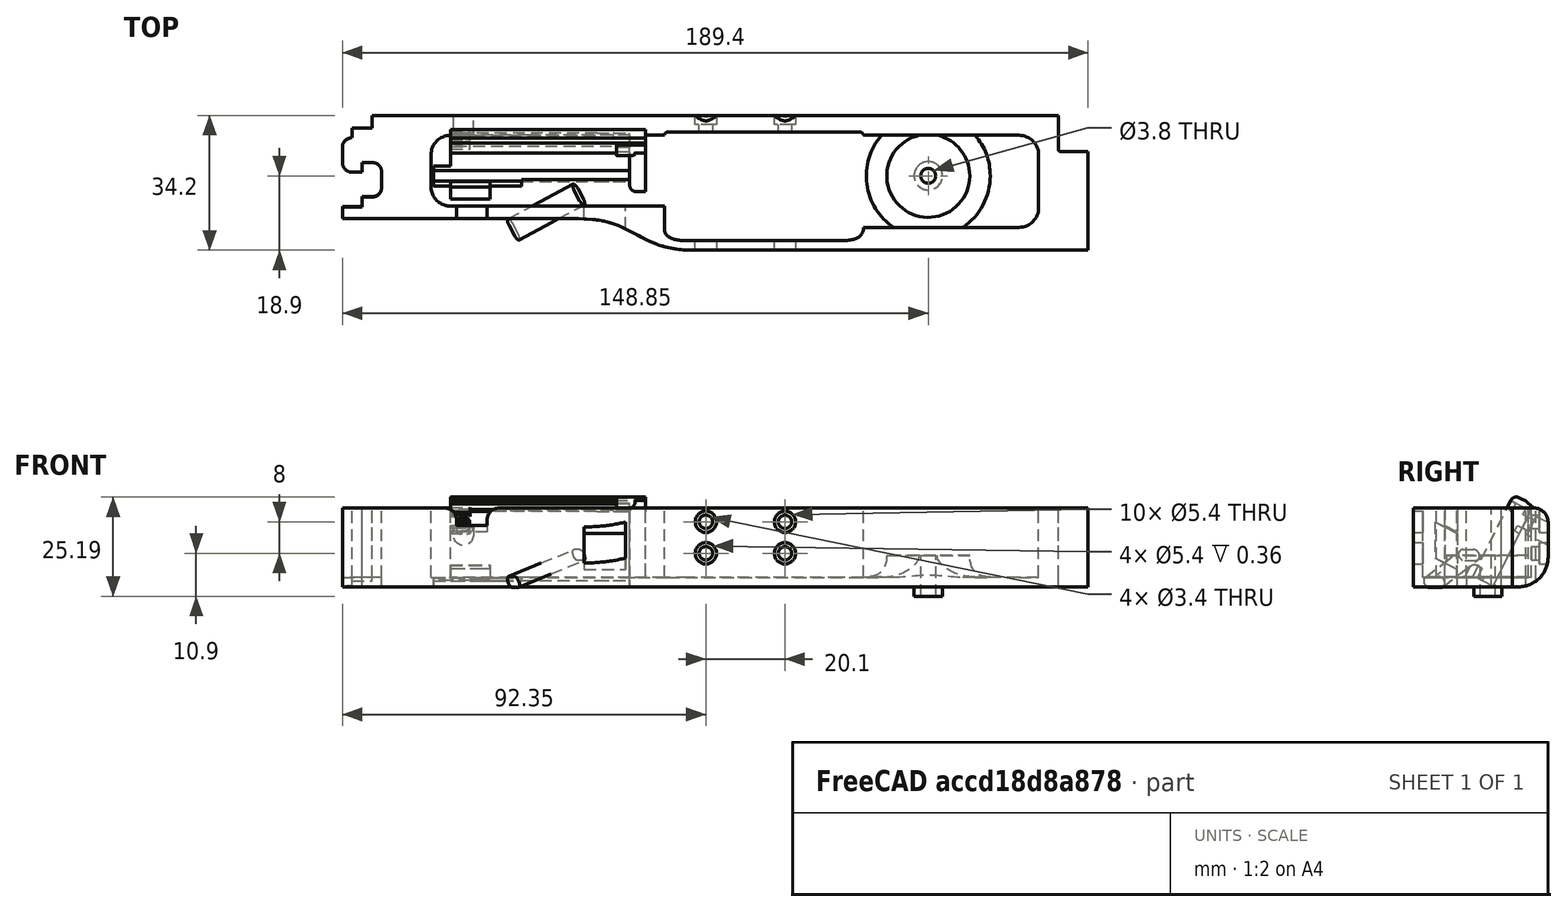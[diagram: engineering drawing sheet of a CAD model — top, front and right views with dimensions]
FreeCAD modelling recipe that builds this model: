
FCSTD DOCUMENT  (FreeCAD 0.19R0.19.2)
Label: v0_996
License: All rights reserved
LicenseURL: http://en.wikipedia.org/wiki/All_rights_reserved
objects: Sketcher::SketchObject×37, Part::Extrusion×31, Part::MultiFuse×19, Part::Box×14, Part::Cut×14, Part::Fillet×13, App::MeasureDistance×4, Part::Cylinder×4, Part::Revolution×1, Mesh::Feature×1
note: 133 computed .brp shape members not serialized (recipe doc carries the construction recipe); baked Part::Feature solids carry a one-line shape summary decoded from their .brp

FEATURE [Sketcher::SketchObject] Sketch
  FullyConstrained = true
  sketch-geometry (36):
    g0: LineSegment StartX=0 StartY=0 StartZ=0 EndX=154.4 EndY=0 EndZ=0
    g1: LineSegment StartX=154.4 StartY=0 StartZ=0 EndX=154.4 EndY=-7.6 EndZ=0
    g2: LineSegment StartX=32.5209 StartY=-26.2 StartZ=0 EndX=-7.5 EndY=-26.2 EndZ=0
    g3-g7: Circle x5 (B-spline internal-alignment scaffolding for g8; pole/knot coordinates omitted)
    g8: BSplineCurve PolesCount=5 KnotsCount=3 Degree=3 IsPeriodic=0
    g9: GeomPoint X=61.85 Y=-33.8 Z=0
    g10: GeomPoint X=47.185 Y=-29.9 Z=0
    g11: GeomPoint X=32.5209 Y=-26.2 Z=0
    g12: Circle CenterX=121.35 CenterY=-14.3 CenterZ=0 NormalX=0 NormalY=0 NormalZ=1 AngleXU=0 Radius=3.25
    g13: LineSegment StartX=-7.5 StartY=-26.2 StartZ=0 EndX=-27.5 EndY=-26.2 EndZ=0
    g14: LineSegment StartX=-20 StartY=0 StartZ=0 EndX=0 EndY=0 EndZ=0
    g15: LineSegment StartX=-25 StartY=-3.1 StartZ=0 EndX=-20 EndY=-3.1 EndZ=0
    g16: LineSegment StartX=-25 StartY=-3.1 StartZ=0 EndX=-25 EndY=-5.6 EndZ=0
    g17: LineSegment StartX=-27.5 StartY=-8.1 StartZ=0 EndX=-27.5 EndY=-11.85 EndZ=0
    g18: ArcOfCircle CenterX=-25 CenterY=-8.1 CenterZ=0 NormalX=0 NormalY=0 NormalZ=1 AngleXU=0 Radius=2.5 StartAngle=1.5708 EndAngle=3.14159
    g19: LineSegment StartX=-25 StartY=-14.35 StartZ=0 EndX=-22.5 EndY=-14.35 EndZ=0
    g20: ArcOfCircle CenterX=-25 CenterY=-11.85 CenterZ=0 NormalX=0 NormalY=0 NormalZ=1 AngleXU=0 Radius=2.5 StartAngle=3.14159 EndAngle=4.71239
    g21: LineSegment StartX=-22.5 StartY=-14.35 StartZ=0 EndX=-22.5 EndY=-11.85 EndZ=0
    g22: LineSegment StartX=-22.5 StartY=-11.85 StartZ=0 EndX=-20 EndY=-11.85 EndZ=0
    g23: ArcOfCircle CenterX=-20 CenterY=-14.35 CenterZ=0 NormalX=0 NormalY=0 NormalZ=1 AngleXU=0 Radius=2.5 StartAngle=8e-16 EndAngle=1.5708
    g24: LineSegment StartX=-17.5 StartY=-14.35 StartZ=0 EndX=-17.5 EndY=-18.1 EndZ=0
    g25: ArcOfCircle CenterX=-20 CenterY=-18.1 CenterZ=0 NormalX=0 NormalY=0 NormalZ=1 AngleXU=0 Radius=2.5 StartAngle=4.71239 EndAngle=6.28319
    g26: LineSegment StartX=-22.5 StartY=-20.6 StartZ=0 EndX=-20 EndY=-20.6 EndZ=0
    g27: LineSegment StartX=-22.5 StartY=-20.6 StartZ=0 EndX=-22.5 EndY=-23.1 EndZ=0
    g28: LineSegment StartX=-27.5 StartY=-23.1 StartZ=0 EndX=-22.5 EndY=-23.1 EndZ=0
    g29: LineSegment StartX=-20 StartY=-3.1 StartZ=0 EndX=-20 EndY=0 EndZ=0
    g30: LineSegment StartX=-27.5 StartY=-23.1 StartZ=0 EndX=-27.5 EndY=-26.2 EndZ=0
    g31: LineSegment StartX=154.4 StartY=-7.6 StartZ=0 EndX=154.4 EndY=-8.6 EndZ=0
    g32: ArcOfCircle CenterX=154.9 CenterY=-8.6 CenterZ=0 NormalX=0 NormalY=0 NormalZ=1 AngleXU=0 Radius=0.5 StartAngle=3.14159 EndAngle=4.71239
    g33: LineSegment StartX=154.9 StartY=-9.1 StartZ=0 EndX=161.9 EndY=-9.1 EndZ=0
    g34: LineSegment StartX=161.9 StartY=-9.1 StartZ=0 EndX=161.9 EndY=-33.8 EndZ=0
    g35: LineSegment StartX=161.9 StartY=-33.8 StartZ=0 EndX=61.85 EndY=-33.8 EndZ=0
  constraints (72):
    c: PointOnObject(g0,g-2)
    c: Horizontal(g0)
    c: Distance(g0) = 154.4
    c: DistanceY(g-1,g0) = 0
    c: Vertical(g1)
    c: Distance(g1) = 7.6
    c: Coincident(g1,g0)
    c: Horizontal(g2)
    c: Block(g2)
    c: Weight(g3) = 1
    c: Coincident(g8,g2)
    c: InternalAlignment(g3-g7 -> g8) x5
    c: InternalAlignment(g9,g8)
    c: InternalAlignment(g10,g8)
    c: InternalAlignment(g11,g8)
    c: Block(g12)
    c: Coincident(g13,g2)
    c: Horizontal(g13)
    c: Distance(g13) = 20
    c: Horizontal(g14)
    c: Distance(g14) = 20
    c: Coincident(g14,g0)
    c: Horizontal(g15)
    c: Vertical(g16)
    c: Coincident(g16,g15)
    c: Vertical(g17)
    c: Coincident(g18,g16)
    c: Block(g18)
    c: Coincident(g17,g18)
    c: Horizontal(g19)
    c: Coincident(g20,g17)
    c: Block(g20)
    c: Block(g19)
    c: Vertical(g21)
    c: Coincident(g21,g19)
    c: Horizontal(g22)
    c: Coincident(g22,g21)
    c: Coincident(g23,g22)
    c: Vertical(g24)
    c: Block(g23)
    c: Coincident(g24,g23)
    c: Coincident(g25,g24)
    c: Block(g25)
    c: Horizontal(g26)
    c: Coincident(g26,g25)
    c: Vertical(g27)
    c: Coincident(g27,g26)
    c: Horizontal(g28)
    c: Coincident(g28,g27)
    c: Block(g15)
    c: Block(g28)
    c: Coincident(g29,g15)
    c: Coincident(g29,g14)
    c: Vertical(g29)
    c: Coincident(g30,g28)
    c: Coincident(g30,g13)
    c: Vertical(g30)
    c: Vertical(g31)
    c: Distance(g31) = 1
    c: Coincident(g31,g1)
    c: Coincident(g32,g31)
    c: Block(g32)
    c: Coincident(g33,g32)
    c: Horizontal(g33)
    c: Coincident(g34,g33)
    c: Vertical(g34)
    c: Block(g34)
    c: Coincident(g35,g34)
    c: Horizontal(g35)
    c: Block(g35)
    c: Coincident(g8,g35)
    c: Block(g8)
FEATURE [Part::Extrusion] Extrude  label="mainBodyBaseExtrude"
  Base = -> Sketch
  Dir = (0,0,1)
  DirMode = 2
  FaceMakerClass = Part::FaceMakerBullseye
  LengthFwd = 2.4
  LengthRev = 0
  Solid = true
  Symmetric = false
FEATURE [Sketcher::SketchObject] Sketch001
  FullyConstrained = true
  sketch-geometry (75):
    g0: ArcOfCircle CenterX=144.4 CenterY=-10 CenterZ=0 NormalX=0 NormalY=0 NormalZ=1 AngleXU=0 Radius=5 StartAngle=4.345e-13 EndAngle=1.5708
    g1: LineSegment StartX=32.5209 StartY=-26.2 StartZ=0 EndX=-7.49911 EndY=-26.2 EndZ=0
    g2: LineSegment StartX=0 StartY=0 StartZ=0 EndX=154.4 EndY=0 EndZ=0
    g3-g7: Circle x5 (B-spline internal-alignment scaffolding for g8; pole/knot coordinates omitted)
    g8: BSplineCurve PolesCount=5 KnotsCount=3 Degree=3 IsPeriodic=0
    g9: GeomPoint X=61.85 Y=-33.8 Z=0
    g10: GeomPoint X=47.1857 Y=-29.9 Z=0
    g11: GeomPoint X=32.5209 Y=-26.2 Z=0
    g12: LineSegment StartX=154.4 StartY=0 StartZ=0 EndX=154.4 EndY=-7.6 EndZ=0
    g13: LineSegment StartX=20 StartY=-5 StartZ=0 EndX=54.35 EndY=-5 EndZ=0
    g14: LineSegment StartX=104.85 StartY=-5 StartZ=0 EndX=144.4 EndY=-5 EndZ=0
    g15: LineSegment StartX=54.35 StartY=-23 StartZ=0 EndX=20 EndY=-23 EndZ=0
    g16: LineSegment StartX=-27.4991 StartY=-26.2 StartZ=0 EndX=-7.49911 EndY=-26.2 EndZ=0
    g17: LineSegment StartX=-20 StartY=0 StartZ=0 EndX=0 EndY=0 EndZ=0
    g18: LineSegment StartX=-27.4991 StartY=-23.2 StartZ=0 EndX=-22.5 EndY=-23.2 EndZ=0
    g19: LineSegment StartX=-22.5 StartY=-20.7 StartZ=0 EndX=-22.5 EndY=-23.2 EndZ=0
    g20: LineSegment StartX=-22.5 StartY=-20.7 StartZ=0 EndX=-20 EndY=-20.7 EndZ=0
    g21: ArcOfCircle CenterX=-20 CenterY=-18.2 CenterZ=0 NormalX=0 NormalY=0 NormalZ=1 AngleXU=0 Radius=2.5 StartAngle=4.71239 EndAngle=6.28319
    g22: LineSegment StartX=-17.5 StartY=-14.4 StartZ=0 EndX=-17.5 EndY=-18.2 EndZ=0
    g23: ArcOfCircle CenterX=-20 CenterY=-14.4 CenterZ=0 NormalX=0 NormalY=0 NormalZ=1 AngleXU=0 Radius=2.5 StartAngle=9e-16 EndAngle=1.5708
    g24: LineSegment StartX=-22.5 StartY=-11.9 StartZ=0 EndX=-20 EndY=-11.9 EndZ=0
    g25: LineSegment StartX=-22.5 StartY=-14.4 StartZ=0 EndX=-22.5 EndY=-11.9 EndZ=0
    g26: LineSegment StartX=-25 StartY=-14.4 StartZ=0 EndX=-22.5 EndY=-14.4 EndZ=0
    g27: ArcOfCircle CenterX=-25 CenterY=-11.9 CenterZ=0 NormalX=0 NormalY=0 NormalZ=1 AngleXU=0 Radius=2.5 StartAngle=3.14159 EndAngle=4.71239
    g28: LineSegment StartX=-27.5 StartY=-8.1 StartZ=0 EndX=-27.5 EndY=-11.9 EndZ=0
    g29: ArcOfCircle CenterX=-25 CenterY=-8.1 CenterZ=0 NormalX=0 NormalY=0 NormalZ=1 AngleXU=0 Radius=2.5 StartAngle=1.5708 EndAngle=3.14159
    g30: LineSegment StartX=-25 StartY=-3.1 StartZ=0 EndX=-25 EndY=-5.6 EndZ=0
    g31: LineSegment StartX=-20 StartY=-3.1 StartZ=0 EndX=-25 EndY=-3.1 EndZ=0
    g32: LineSegment StartX=-20 StartY=0 StartZ=0 EndX=-20 EndY=-3.1 EndZ=0
    g33: LineSegment StartX=-27.4991 StartY=-26.2 StartZ=0 EndX=-27.4991 EndY=-23.2 EndZ=0
    g34: LineSegment StartX=4.09e-14 StartY=-5 StartZ=0 EndX=20 EndY=-5 EndZ=0
    g35: ArcOfCircle CenterX=7.1e-15 CenterY=-18 CenterZ=0 NormalX=0 NormalY=0 NormalZ=1 AngleXU=0 Radius=5 StartAngle=3.14159 EndAngle=4.71239
    g36: ArcOfCircle CenterX=4.26e-14 CenterY=-10 CenterZ=0 NormalX=0 NormalY=0 NormalZ=1 AngleXU=0 Radius=5 StartAngle=1.5708 EndAngle=3.14159
    g37: LineSegment StartX=-5 StartY=-18 StartZ=0 EndX=-5 EndY=-10 EndZ=0
    g38: LineSegment StartX=6.2e-15 StartY=-23 StartZ=0 EndX=20 EndY=-23 EndZ=0
    g39: LineSegment StartX=154.4 StartY=-7.6 StartZ=0 EndX=154.4 EndY=-8.6 EndZ=0
    g40: LineSegment StartX=154.9 StartY=-9.1 StartZ=0 EndX=161.9 EndY=-9.1 EndZ=0
    g41: ArcOfCircle CenterX=154.9 CenterY=-8.6 CenterZ=0 NormalX=0 NormalY=0 NormalZ=1 AngleXU=0 Radius=0.5 StartAngle=3.14159 EndAngle=4.71299
    g42: LineSegment StartX=104.85 StartY=-28.3916 StartZ=0 EndX=144.408 EndY=-28.3916 EndZ=0
    g43: LineSegment StartX=149.4 StartY=-10 StartZ=0 EndX=149.4 EndY=-23.4 EndZ=0
    g44: ArcOfCircle CenterX=144.408 CenterY=-23.4 CenterZ=0 NormalX=0 NormalY=0 NormalZ=1 AngleXU=0 Radius=4.99164 StartAngle=4.71239 EndAngle=6.28319
    g45: LineSegment StartX=104.85 StartY=-28.3916 StartZ=0 EndX=104.85 EndY=-28.7833 EndZ=0
    g46: LineSegment StartX=54.35 StartY=-28.7916 StartZ=0 EndX=54.35 EndY=-23 EndZ=0
    g47: LineSegment StartX=161.9 StartY=-33.8 StartZ=0 EndX=161.9 EndY=-9.1 EndZ=0
    g48: LineSegment StartX=61.85 StartY=-33.8 StartZ=0 EndX=161.9 EndY=-33.8 EndZ=0
    g49: Circle CenterX=54.35 CenterY=-28.7916 CenterZ=0 NormalX=0 NormalY=0 NormalZ=1 AngleXU=0 Radius=1
    g50: Circle CenterX=54.35 CenterY=-31.7916 CenterZ=0 NormalX=0 NormalY=0 NormalZ=1 AngleXU=0 Radius=1
    g51: Circle CenterX=57.35 CenterY=-31.7916 CenterZ=0 NormalX=0 NormalY=0 NormalZ=1 AngleXU=0 Radius=1
    g52: BSplineCurve PolesCount=3 KnotsCount=2 Degree=2 IsPeriodic=0
    g53: GeomPoint X=54.35 Y=-28.7916 Z=0
    g54: GeomPoint X=57.35 Y=-31.7916 Z=0
    g55: Circle CenterX=104.85 CenterY=-28.7833 CenterZ=0 NormalX=0 NormalY=0 NormalZ=1 AngleXU=0 Radius=1
    g56: Circle CenterX=104.85 CenterY=-31.7916 CenterZ=0 NormalX=0 NormalY=0 NormalZ=1 AngleXU=0 Radius=1
    g57: Circle CenterX=101.85 CenterY=-31.7916 CenterZ=0 NormalX=0 NormalY=0 NormalZ=1 AngleXU=0 Radius=1
    g58: BSplineCurve PolesCount=3 KnotsCount=2 Degree=2 IsPeriodic=0
    g59: GeomPoint X=104.85 Y=-28.7833 Z=0
    g60: GeomPoint X=101.85 Y=-31.7916 Z=0
    g61: LineSegment StartX=57.35 StartY=-31.7916 StartZ=0 EndX=101.85 EndY=-31.7916 EndZ=0
    g62: Circle CenterX=54.35 CenterY=-5 CenterZ=0 NormalX=0 NormalY=0 NormalZ=1 AngleXU=0 Radius=1
    g63: Circle CenterX=54.35 CenterY=-4 CenterZ=0 NormalX=0 NormalY=0 NormalZ=1 AngleXU=0 Radius=1
    g64: Circle CenterX=55.15 CenterY=-4 CenterZ=0 NormalX=0 NormalY=0 NormalZ=1 AngleXU=0 Radius=1
    g65: BSplineCurve PolesCount=3 KnotsCount=2 Degree=2 IsPeriodic=0
    g66: GeomPoint X=54.35 Y=-5 Z=0
    g67: GeomPoint X=55.15 Y=-4 Z=0
    g68: Circle CenterX=104.85 CenterY=-5 CenterZ=0 NormalX=0 NormalY=0 NormalZ=1 AngleXU=0 Radius=1
    g69: Circle CenterX=104.85 CenterY=-4 CenterZ=0 NormalX=0 NormalY=0 NormalZ=1 AngleXU=0 Radius=1
    g70: Circle CenterX=104.05 CenterY=-4 CenterZ=0 NormalX=0 NormalY=0 NormalZ=1 AngleXU=0 Radius=1
    g71: BSplineCurve PolesCount=3 KnotsCount=2 Degree=2 IsPeriodic=0
    g72: GeomPoint X=104.85 Y=-5 Z=0
    g73: GeomPoint X=104.05 Y=-4 Z=0
    g74: LineSegment StartX=104.05 StartY=-4 StartZ=0 EndX=55.15 EndY=-4 EndZ=0
  constraints (156):
    c: PointOnObject(g2,g-2)
    c: DistanceY(g-1,g2) = 0
    c: Block(g0)
    c: Horizontal(g1)
    c: Distance(g1) = 40.02
    c: Horizontal(g2)
    c: Block(g2)
    c: Weight(g3) = 1
    c: Equal(g3, g4-g7) x4
    c: Coincident(g8,g1)
    c: InternalAlignment(g3-g7 -> g8) x5
    c: InternalAlignment(g9,g8)
    c: InternalAlignment(g10,g8)
    c: InternalAlignment(g11,g8)
    c: Vertical(g12)
    c: Coincident(g12,g2)
    c: Distance(g12) = 7.6
    c: Block(g12)
    c: Horizontal(g13)
    c: Coincident(g14,g0)
    c: Horizontal(g14)
    c: Horizontal(g15)
    c: Horizontal(g16)
    c: Distance(g16) = 20
    c: Coincident(g1,g16)
    c: Horizontal(g17)
    c: Distance(g17) = 20
    c: Coincident(g17,g2)
    c: Horizontal(g31)
    c: Vertical(g30)
    c: Coincident(g29,g30)
    c: Vertical(g28)
    c: Block(g29)
    c: Coincident(g27,g28)
    c: Block(g27)
    c: Horizontal(g26)
    c: Coincident(g26,g27)
    c: Vertical(g25)
    c: Coincident(g25,g26)
    c: Horizontal(g24)
    c: Coincident(g23,g24)
    c: Block(g23)
    c: Vertical(g22)
    c: Coincident(g21,g22)
    c: Block(g21)
    c: Horizontal(g20)
    c: Coincident(g20,g21)
    c: Vertical(g19)
    c: Coincident(g19,g20)
    c: Horizontal(g18)
    c: Coincident(g18,g19)
    c: Coincident(g32,g17)
    c: Coincident(g32,g31)
    c: Vertical(g32)
    c: Coincident(g33,g16)
    c: Coincident(g33,g18)
    c: Vertical(g33)
    c: Block(g33)
    c: Block(g18)
    c: Block(g22)
    c: Block(g26)
    c: Block(g25)
    c: Block(g24)
    c: Block(g28)
    c: Block(g31)
    c: Block(g30)
    c: Horizontal(g34)
    c: Distance(g34) = 20
    c: Block(g35)
    c: Block(g36)
    c: Coincident(g37,g35)
    c: Coincident(g37,g36)
    c: Vertical(g37)
    c: Coincident(g38,g35)
    c: Coincident(g38,g15)
    c: Horizontal(g38)
    c: Block(g38)
    c: Block(g34)
    c: Block(g13)
    c: Vertical(g39)
    c: Distance(g39) = 1
    c: Coincident(g39,g12)
    c: Horizontal(g40)
    c: Coincident(g41,g39)
    c: Coincident(g41,g40)
    c: Block(g39)
    c: Block(g41)
    c: Horizontal(g42)
    c: Vertical(g43)
    c: Distance(g43) = 13.4
    c: Coincident(g43,g0)
    c: Block(g42)
    c: Block(g43)
    c: Coincident(g44,g43)
    c: Coincident(g44,g42)
    c: Block(g44)
    c: Distance(g15) = 34.35
    c: Coincident(g45,g42)
    c: Vertical(g45)
    c: Coincident(g46,g15)
    c: Vertical(g46)
    c: Coincident(g47,g40)
    c: Vertical(g47)
    c: Block(g47)
    c: Coincident(g48,g47)
    c: Horizontal(g48)
    c: Block(g48)
    c: Coincident(g8,g48)
    c: Block(g8)
    c: Coincident(g52,g46)
    c: Weight(g49) = 1
    c: Equal(g49,g50)
    c: Equal(g49,g51)
    c: InternalAlignment(g49,g52)
    c: InternalAlignment(g50,g52)
    c: InternalAlignment(g51,g52)
    c: InternalAlignment(g53,g52)
    c: InternalAlignment(g54,g52)
    c: Coincident(g58,g45)
    c: Weight(g55) = 1
    c: Equal(g55,g56)
    c: Equal(g55,g57)
    c: InternalAlignment(g55,g58)
    c: InternalAlignment(g56,g58)
    c: InternalAlignment(g57,g58)
    c: InternalAlignment(g59,g58)
    c: InternalAlignment(g60,g58)
    c: Block(g58)
    c: Block(g52)
    c: Coincident(g61,g52)
    c: Coincident(g61,g58)
    c: Horizontal(g61)
    c: Block(g14)
    c: Coincident(g65,g13)
    c: Weight(g62) = 1
    c: Equal(g62,g63)
    c: Equal(g62,g64)
    c: InternalAlignment(g62,g65)
    c: InternalAlignment(g63,g65)
    c: InternalAlignment(g64,g65)
    c: InternalAlignment(g66,g65)
    c: InternalAlignment(g67,g65)
    c: Block(g65)
    c: Coincident(g71,g14)
    c: Weight(g68) = 1
    c: Equal(g68,g69)
    c: Equal(g68,g70)
    c: InternalAlignment(g68,g71)
    c: InternalAlignment(g69,g71)
    c: InternalAlignment(g70,g71)
    c: InternalAlignment(g72,g71)
    c: InternalAlignment(g73,g71)
    c: Block(g71)
    c: Coincident(g74,g71)
    c: Coincident(g74,g65)
    c: Horizontal(g74)
FEATURE [Sketcher::SketchObject] Sketch005
  FullyConstrained = true
  Placement = pos=(0,0,0) rot=(1,0,0;1.5708rad)
  sketch-geometry (4):
    g0: Circle CenterX=84.95 CenterY=16.5 CenterZ=0 NormalX=0 NormalY=0 NormalZ=1 AngleXU=0 Radius=1.7
    g1: Circle CenterX=84.95 CenterY=8.5 CenterZ=0 NormalX=0 NormalY=0 NormalZ=1 AngleXU=0 Radius=1.7
    g2: Circle CenterX=64.85 CenterY=8.5 CenterZ=0 NormalX=0 NormalY=0 NormalZ=1 AngleXU=0 Radius=1.7
    g3: Circle CenterX=64.85 CenterY=16.5 CenterZ=0 NormalX=0 NormalY=0 NormalZ=1 AngleXU=0 Radius=1.7
  constraints (4):
    c: Block(g0)
    c: Block(g1)
    c: Block(g2)
    c: Block(g3)
FEATURE [Part::Extrusion] Extrude004  label="removeFromMainBodyToCreateScrewHolesForSolenoidExtrude004"
  Base = -> Sketch005
  Dir = (0,-1,1.1e-15)
  DirMode = 2
  FaceMakerClass = Part::FaceMakerBullseye
  LengthFwd = 10
  LengthRev = 0
  Solid = true
  Symmetric = false
FEATURE [Sketcher::SketchObject] Sketch004
  FullyConstrained = true
  Placement = pos=(0,0,0) rot=(1,0,0;1.5708rad)
  sketch-geometry (12):
    g0: LineSegment StartX=15.75 StartY=2.5 StartZ=0 EndX=15.75 EndY=0 EndZ=0
    g1: Circle CenterX=15.75 CenterY=2.5 CenterZ=0 NormalX=0 NormalY=0 NormalZ=1 AngleXU=0 Radius=1
    g2: Circle CenterX=10.55 CenterY=2.5 CenterZ=0 NormalX=0 NormalY=0 NormalZ=1 AngleXU=0 Radius=1
    g3: Circle CenterX=10.55 CenterY=8 CenterZ=0 NormalX=0 NormalY=0 NormalZ=1 AngleXU=0 Radius=1
    g4: BSplineCurve PolesCount=3 KnotsCount=2 Degree=2 IsPeriodic=0
    g5: GeomPoint X=15.75 Y=2.5 Z=0
    g6: GeomPoint X=10.55 Y=8 Z=0
    g7: LineSegment StartX=1.9 StartY=8 StartZ=0 EndX=10.55 EndY=8 EndZ=0
    g8: LineSegment StartX=1.9 StartY=-2.4 StartZ=0 EndX=1.9 EndY=8 EndZ=0
    g9: LineSegment StartX=3.30092 StartY=-2.4 StartZ=0 EndX=3.30092 EndY=0 EndZ=0
    g10: LineSegment StartX=15.75 StartY=0 StartZ=0 EndX=3.30092 EndY=0 EndZ=0
    g11: LineSegment StartX=3.30092 StartY=-2.4 StartZ=0 EndX=1.9 EndY=-2.4 EndZ=0
  constraints (26):
    c: Vertical(g0)
    c: Distance(g0) = 2.5
    c: Coincident(g4,g0)
    c: Weight(g1) = 1
    c: Equal(g1,g2)
    c: Equal(g1,g3)
    c: InternalAlignment(g1,g4)
    c: InternalAlignment(g2,g4)
    c: InternalAlignment(g3,g4)
    c: InternalAlignment(g5,g4)
    c: InternalAlignment(g6,g4)
    c: Block(g4)
    c: Coincident(g7,g4)
    c: Horizontal(g7)
    c: Vertical(g8)
    c: Coincident(g8,g7)
    c: Block(g8)
    c: Vertical(g9)
    c: Coincident(g10,g0)
    c: PointOnObject(g10,g-1)
    c: Horizontal(g10)
    c: Coincident(g10,g9)
    c: Block(g9)
    c: Coincident(g11,g9)
    c: Coincident(g11,g8)
    c: Horizontal(g11)
FEATURE [Sketcher::SketchObject] Sketch007
  FullyConstrained = true
  Placement = pos=(0,-14.3,2.37) rot=(-1,0,0;2.03453rad)
  sketch-geometry (6):
    g0: LineSegment StartX=0 StartY=0 StartZ=0 EndX=45.5 EndY=0 EndZ=0
    g1: LineSegment StartX=0 StartY=0 StartZ=0 EndX=0 EndY=-21.2 EndZ=0
    g2: LineSegment StartX=45.5 StartY=0 StartZ=0 EndX=49.5 EndY=0 EndZ=0
    g3: LineSegment StartX=49.5 StartY=0 StartZ=0 EndX=49.5 EndY=-21.2 EndZ=0
    g4: LineSegment StartX=49.5 StartY=-21.2 StartZ=0 EndX=0 EndY=-21.2 EndZ=0
    g5: Circle CenterX=3.25 CenterY=-18.05 CenterZ=0 NormalX=0 NormalY=0 NormalZ=1 AngleXU=0 Radius=1.6
  constraints (15):
    c: Coincident(g0,g-1)
    c: Horizontal(g0)
    c: Distance(g0) = 45.5
    c: Coincident(g1,g0)
    c: Vertical(g1)
    c: Horizontal(g2)
    c: Distance(g2) = 4
    c: Coincident(g2,g0)
    c: Coincident(g3,g2)
    c: Vertical(g3)
    c: Block(g3)
    c: Coincident(g4,g3)
    c: Horizontal(g4)
    c: Coincident(g4,g1)
    c: Block(g5)
FEATURE [Part::Extrusion] Extrude005  label="solenoidDriverHolderExtrude005"
  Base = -> Sketch007
  Dir = (0,0.894389,-0.447291)
  DirMode = 2
  FaceMakerClass = Part::FaceMakerBullseye
  LengthFwd = 10
  LengthRev = 0
  Placement = pos=(0,0,-2) rot=(0,0,1;0rad)
  Solid = true
  Symmetric = false
FEATURE [Sketcher::SketchObject] Sketch008
  FullyConstrained = false
  Placement = pos=(0,-4.3,-2.6) rot=(-1,0,0;2.03453rad)
  sketch-geometry (1):
    g0: Circle CenterX=42.25 CenterY=-3.15 CenterZ=0 NormalX=0 NormalY=0 NormalZ=1 AngleXU=0 Radius=4.5
FEATURE [Sketcher::SketchObject] Sketch009
  FullyConstrained = true
  Placement = pos=(0,-4.3,-2.6) rot=(-1,0,0;2.03453rad)
  sketch-geometry (1):
    g0: Circle CenterX=3.25 CenterY=-18.0217 CenterZ=0 NormalX=0 NormalY=0 NormalZ=1 AngleXU=0 Radius=2.8
  constraints (1):
    c: Block(g0)
FEATURE [Sketcher::SketchObject] Sketch010
  FullyConstrained = true
  Placement = pos=(0,-14.3,2.37) rot=(-1,0,0;2.03453rad)
  sketch-geometry (1):
    g0: Circle CenterX=3.25 CenterY=-18.05 CenterZ=0 NormalX=0 NormalY=0 NormalZ=1 AngleXU=0 Radius=1.6
  constraints (1):
    c: Block(g0)
FEATURE [Part::Extrusion] Extrude008  label="removeFromScrewHole3"
  Base = -> Sketch010
  Dir = (0,0.894389,-0.447291)
  DirMode = 2
  FaceMakerClass = Part::FaceMakerBullseye
  LengthFwd = -25
  LengthRev = 0
  Placement = pos=(0,4,-4) rot=(0,0,1;0rad)
  Solid = true
  Symmetric = false
FEATURE [Sketcher::SketchObject] Sketch011
  FullyConstrained = true
  Placement = pos=(0,-14.3,2.37) rot=(-1,0,0;2.03453rad)
  sketch-geometry (4):
    g0: LineSegment StartX=49.5 StartY=-21.2 StartZ=0 EndX=49.5 EndY=-22.8 EndZ=0
    g1: LineSegment StartX=49.5 StartY=-22.8 StartZ=0 EndX=0.002238 EndY=-22.8 EndZ=0
    g2: LineSegment StartX=0.002238 StartY=-21.2 StartZ=0 EndX=0.002238 EndY=-22.8 EndZ=0
    g3: LineSegment StartX=49.5 StartY=-21.2 StartZ=0 EndX=0.002238 EndY=-21.2 EndZ=0
  constraints (10):
    c: Vertical(g0)
    c: Distance(g0) = 1.6
    c: Coincident(g1,g0)
    c: Horizontal(g1)
    c: Vertical(g2)
    c: Coincident(g2,g1)
    c: Coincident(g3,g0)
    c: Coincident(g3,g2)
    c: Horizontal(g3)
    c: Block(g3)
FEATURE [Part::Extrusion] Extrude009  label="solenoidDriverTopLipFront"
  Base = -> Sketch011
  Dir = (0,0.894389,-0.447291)
  DirMode = 2
  FaceMakerClass = Part::FaceMakerBullseye
  LengthFwd = -2
  LengthRev = 0
  Placement = pos=(0,-2.9,-0.35) rot=(0,0,1;0rad)
  Solid = true
  Symmetric = false
FEATURE [Sketcher::SketchObject] Sketch012
  FullyConstrained = true
  Placement = pos=(0,-14.3,2.37) rot=(-1,0,0;2.03453rad)
  sketch-geometry (4):
    g0: LineSegment StartX=49.5 StartY=-21.2 StartZ=0 EndX=49.5 EndY=-22.8 EndZ=0
    g1: LineSegment StartX=49.5 StartY=-22.8 StartZ=0 EndX=0.002238 EndY=-22.8 EndZ=0
    g2: LineSegment StartX=0.002238 StartY=-21.2 StartZ=0 EndX=0.002238 EndY=-22.8 EndZ=0
    g3: LineSegment StartX=49.5 StartY=-21.2 StartZ=0 EndX=0.002238 EndY=-21.2 EndZ=0
  constraints (10):
    c: Vertical(g0)
    c: Distance(g0) = 1.6
    c: Coincident(g1,g0)
    c: Horizontal(g1)
    c: Vertical(g2)
    c: Coincident(g2,g1)
    c: Coincident(g3,g0)
    c: Coincident(g3,g2)
    c: Horizontal(g3)
    c: Block(g3)
FEATURE [Part::Extrusion] Extrude010  label="solenoidDriverTopLipLowerExtrude010"
  Base = -> Sketch012
  Dir = (0,0.894389,-0.447291)
  DirMode = 2
  FaceMakerClass = Part::FaceMakerBullseye
  LengthFwd = 5.05
  LengthRev = 0
  Solid = true
  Symmetric = false
FEATURE [Sketcher::SketchObject] Sketch015
  FullyConstrained = true
  Placement = pos=(0,-14.3,2.37) rot=(-1,0,0;2.03453rad)
  sketch-geometry (4):
    g0: LineSegment StartX=0 StartY=1.5 StartZ=0 EndX=0 EndY=0 EndZ=0
    g1: LineSegment StartX=0 StartY=1.5 StartZ=0 EndX=5 EndY=1.5 EndZ=0
    g2: LineSegment StartX=5 StartY=1.5 StartZ=0 EndX=5 EndY=0 EndZ=0
    g3: LineSegment StartX=0 StartY=0 StartZ=0 EndX=5 EndY=0 EndZ=0
  constraints (13):
    c: Vertical(g0)
    c: Distance(g0) = 1.5
    c: Horizontal(g1)
    c: Distance(g1) = 5
    c: Coincident(g1,g0)
    c: Vertical(g2)
    c: Distance(g2) = 1.5
    c: Coincident(g2,g1)
    c: Block(g1)
    c: Block(g2)
    c: Block(g0)
    c: Coincident(g3,g0)
    c: Coincident(g3,g2)
FEATURE [Part::Extrusion] Extrude013  label="solenoidDriverBottomLipTopExtrude012"
  Base = -> Sketch015
  Dir = (0,0.894389,-0.447291)
  DirMode = 2
  FaceMakerClass = Part::FaceMakerBullseye
  LengthFwd = -6.5
  LengthRev = 0
  Placement = pos=(0,-14.15,19.65) rot=(1,0,0;1.5708rad)
  Solid = true
  Symmetric = false
FEATURE [Sketcher::SketchObject] Sketch016
  FullyConstrained = true
  Placement = pos=(0,0,0) rot=(1,0,0;1.5708rad)
  sketch-geometry (4):
    g0: Circle CenterX=84.15 CenterY=16.5 CenterZ=0 NormalX=0 NormalY=0 NormalZ=1 AngleXU=0 Radius=2.7
    g1: Circle CenterX=64.05 CenterY=16.5 CenterZ=0 NormalX=0 NormalY=0 NormalZ=1 AngleXU=0 Radius=2.7
    g2: Circle CenterX=64.05 CenterY=8.5 CenterZ=0 NormalX=0 NormalY=0 NormalZ=1 AngleXU=0 Radius=2.7
    g3: Circle CenterX=84.15 CenterY=8.5 CenterZ=0 NormalX=0 NormalY=0 NormalZ=1 AngleXU=0 Radius=2.7
  constraints (4):
    c: Block(g0)
    c: Block(g1)
    c: Block(g3)
    c: Block(g2)
FEATURE [Part::Extrusion] Extrude014  label="removeFromMainBodyToCreateScrewHoleCounterSinks"
  Base = -> Sketch016
  Dir = (0,-1,1.1e-15)
  DirMode = 2
  FaceMakerClass = Part::FaceMakerBullseye
  LengthFwd = 1.9
  LengthRev = 0
  Placement = pos=(0.8,-0.36,0) rot=(0,0,1;0rad)
  Solid = true
  Symmetric = false
FEATURE [Part::Extrusion] Extrude015  label="removeFromScrewHole2Extrude007"
  Base = -> Sketch009
  Dir = (0,0.894389,-0.447291)
  DirMode = 2
  FaceMakerClass = Part::FaceMakerBullseye
  LengthFwd = 10
  LengthRev = 0
  Placement = pos=(0,-8,2) rot=(0,0,1;0rad)
  Solid = true
  Symmetric = false
FEATURE [Sketcher::SketchObject] Sketch017
  FullyConstrained = true
  Placement = pos=(0,-14.3,2.37) rot=(-1,0,0;2.03453rad)
  sketch-geometry (4):
    g0: LineSegment StartX=0 StartY=1.5 StartZ=0 EndX=0 EndY=0 EndZ=0
    g1: LineSegment StartX=0 StartY=1.5 StartZ=0 EndX=5 EndY=1.5 EndZ=0
    g2: LineSegment StartX=5 StartY=1.5 StartZ=0 EndX=5 EndY=0 EndZ=0
    g3: LineSegment StartX=0 StartY=0 StartZ=0 EndX=5 EndY=0 EndZ=0
  constraints (13):
    c: Vertical(g0)
    c: Distance(g0) = 1.5
    c: Horizontal(g1)
    c: Distance(g1) = 5
    c: Coincident(g1,g0)
    c: Vertical(g2)
    c: Distance(g2) = 1.5
    c: Coincident(g2,g1)
    c: Block(g1)
    c: Block(g2)
    c: Block(g0)
    c: Coincident(g3,g0)
    c: Coincident(g3,g2)
FEATURE [Part::Extrusion] Extrude016  label="solenoidDriverBottomLipTopExtrude013"
  Base = -> Sketch017
  Dir = (0,0.894389,-0.447291)
  DirMode = 2
  FaceMakerClass = Part::FaceMakerBullseye
  LengthFwd = -6.5
  LengthRev = 0
  Placement = pos=(0,-15.45,20.3) rot=(1,0,0;1.5708rad)
  Solid = true
  Symmetric = false
FEATURE [Part::Fillet] Fillet005  label="solenoidDriverBottomLipTopFillet005"
  Base = -> Extrude016
  Edges = 1 edges r=1.4: [Edge6]
FEATURE [Sketcher::SketchObject] Sketch018
  FullyConstrained = true
  Placement = pos=(38.5,-14.3,2.37) rot=(-1,0,0;2.03453rad)
  sketch-geometry (4):
    g0: LineSegment StartX=11 StartY=0 StartZ=0 EndX=11 EndY=1.5 EndZ=0
    g1: LineSegment StartX=11 StartY=0 StartZ=0 EndX=3.6 EndY=0 EndZ=0
    g2: LineSegment StartX=3.6 StartY=0 StartZ=0 EndX=3.6 EndY=1.5 EndZ=0
    g3: LineSegment StartX=11 StartY=1.5 StartZ=0 EndX=3.6 EndY=1.5 EndZ=0
  constraints (12):
    c: PointOnObject(g0,g-1)
    c: Vertical(g0)
    c: Distance(g0) = 1.5
    c: Horizontal(g1)
    c: Distance(g1) = 7.4
    c: Coincident(g1,g0)
    c: Block(g0)
    c: Coincident(g2,g1)
    c: Vertical(g2)
    c: Coincident(g3,g0)
    c: Horizontal(g3)
    c: Coincident(g2,g3)
FEATURE [Part::Extrusion] Extrude017
  Base = -> Sketch018
  Dir = (0,0.894389,-0.447291)
  DirMode = 2
  FaceMakerClass = Part::FaceMakerBullseye
  LengthFwd = 4
  LengthRev = 0
  Placement = pos=(0,-8.212,34.025) rot=(1,0,0;1.5708rad)
  Solid = true
  Symmetric = false
FEATURE [Sketcher::SketchObject] Sketch019
  FullyConstrained = true
  Placement = pos=(0,0,0) rot=(1,0,0;1.5708rad)
  sketch-geometry (4):
    g0: Circle CenterX=84.95 CenterY=8.5 CenterZ=0 NormalX=0 NormalY=0 NormalZ=1 AngleXU=0 Radius=2.7
    g1: Circle CenterX=64.85 CenterY=8.5 CenterZ=0 NormalX=0 NormalY=0 NormalZ=1 AngleXU=0 Radius=2.7
    g2: Circle CenterX=64.85 CenterY=16.5 CenterZ=0 NormalX=0 NormalY=0 NormalZ=1 AngleXU=0 Radius=2.7
    g3: Circle CenterX=84.95 CenterY=16.5 CenterZ=0 NormalX=0 NormalY=0 NormalZ=1 AngleXU=0 Radius=2.7
  constraints (4):
    c: Block(g3)
    c: Block(g2)
    c: Block(g0)
    c: Block(g1)
FEATURE [Part::Extrusion] Extrude019  label="removeSolenoidAdjusterHoles"
  Base = -> Sketch019
  Dir = (0,-1,1.1e-15)
  DirMode = 2
  FaceMakerClass = Part::FaceMakerBullseye
  LengthFwd = 6
  LengthRev = 0
  Placement = pos=(0,-30,0) rot=(0,0,1;0rad)
  Solid = true
  Symmetric = false
FEATURE [Sketcher::SketchObject] Sketch020
  FullyConstrained = true
  Placement = pos=(0,-14.3,2.37) rot=(-1,0,0;2.03453rad)
  sketch-geometry (6):
    g0: LineSegment StartX=45.5 StartY=-21.2 StartZ=0 EndX=49.5 EndY=-21.2 EndZ=0
    g1: LineSegment StartX=45.5 StartY=0 StartZ=0 EndX=49.5 EndY=0 EndZ=0
    g2: LineSegment StartX=49.5 StartY=0 StartZ=0 EndX=49.5 EndY=-21.2 EndZ=0
    g3: LineSegment StartX=4 StartY=0 StartZ=0 EndX=4 EndY=-21.2 EndZ=0
    g4: LineSegment StartX=45.5 StartY=-21.2 StartZ=0 EndX=4 EndY=-21.2 EndZ=0
    g5: LineSegment StartX=4 StartY=0 StartZ=0 EndX=45.5 EndY=0 EndZ=0
  constraints (16):
    c: Horizontal(g0)
    c: Distance(g0) = 4
    c: Horizontal(g1)
    c: Distance(g1) = 4
    c: Coincident(g2,g1)
    c: Coincident(g2,g0)
    c: Vertical(g2)
    c: Block(g2)
    c: Vertical(g3)
    c: Coincident(g4,g0)
    c: Horizontal(g4)
    c: Coincident(g4,g3)
    c: Coincident(g5,g1)
    c: Horizontal(g5)
    c: Block(g3)
    c: Block(g5)
FEATURE [Part::Box] Box  label="Cube"
  AttacherType = Attacher::AttachEngine3D
  Height = 10
  Length = 190
  Placement = pos=(-30,0,0) rot=(0,0,1;0rad)
  Width = 10
FEATURE [Part::Fillet] Fillet008
  Base = -> Box
  Edges = 1 edges r=7.5: [Edge11]
FEATURE [Part::Box] Box001  label="Cube001"
  AttacherType = Attacher::AttachEngine3D
  Height = 10
  Length = 190
  Placement = pos=(-35,0,0) rot=(0,0,1;0rad)
  Width = 10
FEATURE [Part::Cut] Cut  label="filletMain"
  Base = -> Box001
  Placement = pos=(0,-10,0) rot=(0,0,1;0rad)
  Tool = -> Fillet008
FEATURE [Part::Box] Box002  label="Cube002"
  AttacherType = Attacher::AttachEngine3D
  Height = 30
  Length = 190
  Placement = pos=(-20,0,0) rot=(0,0,1;0rad)
  Width = 10
FEATURE [Part::Box] Box003  label="Cube003"
  AttacherType = Attacher::AttachEngine3D
  Height = 10
  Length = 190
  Placement = pos=(-90,-50,-10) rot=(0,0,1;0rad)
  Width = 50
FEATURE [Sketcher::SketchObject] Sketch021
  FullyConstrained = true
  Placement = pos=(0,-14.3,2.37) rot=(-1,0,0;2.03453rad)
  sketch-geometry (6):
    g0: LineSegment StartX=41.65 StartY=-3.15 StartZ=0 EndX=38.95 EndY=-3.15 EndZ=0
    g1: LineSegment StartX=36.25 StartY=-3.15 StartZ=0 EndX=38.95 EndY=-3.15 EndZ=0
    g2: LineSegment StartX=41.65 StartY=-3.15 StartZ=0 EndX=41.65 EndY=-7.15 EndZ=0
    g3: LineSegment StartX=38.95 StartY=-7.15 StartZ=0 EndX=41.65 EndY=-7.15 EndZ=0
    g4: LineSegment StartX=38.95 StartY=-7.15 StartZ=0 EndX=36.25 EndY=-7.15 EndZ=0
    g5: LineSegment StartX=36.25 StartY=-3.15 StartZ=0 EndX=36.25 EndY=-7.15 EndZ=0
  constraints (16):
    c: Horizontal(g0)
    c: Distance(g0) = 2.7
    c: Horizontal(g1)
    c: Distance(g1) = 2.7
    c: Coincident(g1,g0)
    c: Block(g0)
    c: Coincident(g2,g0)
    c: Vertical(g2)
    c: Horizontal(g3)
    c: Coincident(g3,g2)
    c: Horizontal(g4)
    c: Coincident(g5,g1)
    c: Vertical(g5)
    c: Coincident(g5,g4)
    c: Block(g3)
    c: Block(g4)
FEATURE [Sketcher::SketchObject] Sketch022
  FullyConstrained = true
  Placement = pos=(0,-14.3,2.37) rot=(-1,0,0;2.03453rad)
  sketch-geometry (6):
    g0: LineSegment StartX=41.65 StartY=-3.15 StartZ=0 EndX=38.95 EndY=-3.15 EndZ=0
    g1: LineSegment StartX=36.25 StartY=-3.15 StartZ=0 EndX=38.95 EndY=-3.15 EndZ=0
    g2: LineSegment StartX=41.65 StartY=-3.15 StartZ=0 EndX=41.65 EndY=-7.15 EndZ=0
    g3: LineSegment StartX=38.95 StartY=-7.15 StartZ=0 EndX=41.65 EndY=-7.15 EndZ=0
    g4: LineSegment StartX=38.95 StartY=-7.15 StartZ=0 EndX=36.25 EndY=-7.15 EndZ=0
    g5: LineSegment StartX=36.25 StartY=-3.15 StartZ=0 EndX=36.25 EndY=-7.15 EndZ=0
  constraints (16):
    c: Horizontal(g0)
    c: Distance(g0) = 2.7
    c: Horizontal(g1)
    c: Distance(g1) = 2.7
    c: Coincident(g1,g0)
    c: Block(g0)
    c: Coincident(g2,g0)
    c: Vertical(g2)
    c: Horizontal(g3)
    c: Coincident(g3,g2)
    c: Horizontal(g4)
    c: Coincident(g5,g1)
    c: Vertical(g5)
    c: Coincident(g5,g4)
    c: Block(g3)
    c: Block(g4)
FEATURE [Sketcher::SketchObject] Sketch024
  FullyConstrained = true
  Placement = pos=(0,-14.3,2.37) rot=(-1,0,0;2.03453rad)
  sketch-geometry (4):
    g0: LineSegment StartX=49.5 StartY=-21.2 StartZ=0 EndX=49.5 EndY=-22.8 EndZ=0
    g1: LineSegment StartX=49.5 StartY=-22.8 StartZ=0 EndX=0.002238 EndY=-22.8 EndZ=0
    g2: LineSegment StartX=0.002238 StartY=-21.2 StartZ=0 EndX=0.002238 EndY=-22.8 EndZ=0
    g3: LineSegment StartX=49.5 StartY=-21.2 StartZ=0 EndX=0.002238 EndY=-21.2 EndZ=0
  constraints (10):
    c: Vertical(g0)
    c: Distance(g0) = 1.6
    c: Coincident(g1,g0)
    c: Horizontal(g1)
    c: Vertical(g2)
    c: Coincident(g2,g1)
    c: Coincident(g3,g0)
    c: Coincident(g3,g2)
    c: Horizontal(g3)
    c: Block(g3)
FEATURE [Sketcher::SketchObject] Sketch025
  FullyConstrained = true
  Placement = pos=(0,-14.3,2.37) rot=(-1,0,0;2.03453rad)
  sketch-geometry (4):
    g0: LineSegment StartX=0 StartY=1.5 StartZ=0 EndX=0 EndY=0 EndZ=0
    g1: LineSegment StartX=0 StartY=1.5 StartZ=0 EndX=5 EndY=1.5 EndZ=0
    g2: LineSegment StartX=5 StartY=1.5 StartZ=0 EndX=5 EndY=0 EndZ=0
    g3: LineSegment StartX=0 StartY=0 StartZ=0 EndX=5 EndY=0 EndZ=0
  constraints (13):
    c: Vertical(g0)
    c: Distance(g0) = 1.5
    c: Horizontal(g1)
    c: Distance(g1) = 5
    c: Coincident(g1,g0)
    c: Vertical(g2)
    c: Distance(g2) = 1.5
    c: Coincident(g2,g1)
    c: Block(g1)
    c: Block(g2)
    c: Block(g0)
    c: Coincident(g3,g0)
    c: Coincident(g3,g2)
FEATURE [Part::Extrusion] Extrude022  label="solenoidDriverBottomLipTopExtrude014"
  Base = -> Sketch025
  Dir = (0,0.894389,-0.447291)
  DirMode = 2
  FaceMakerClass = Part::FaceMakerBullseye
  LengthFwd = -6.5
  LengthRev = 0
  Placement = pos=(0,-15.45,20.3) rot=(1,0,0;1.5708rad)
  Solid = true
  Symmetric = false
FEATURE [Part::Fillet] Fillet013  label="solenoidDriverBottomLipTopFillet006"
  Base = -> Extrude022
  Edges = 1 edges r=1.4: [Edge6]
  Placement = pos=(5,0,0) rot=(0,0,1;0rad)
FEATURE [Sketcher::SketchObject] Sketch026
  FullyConstrained = true
  Placement = pos=(0,-14.3,2.37) rot=(-1,0,0;2.03453rad)
  sketch-geometry (4):
    g0: LineSegment StartX=0 StartY=1.5 StartZ=0 EndX=0 EndY=0 EndZ=0
    g1: LineSegment StartX=0 StartY=1.5 StartZ=0 EndX=5 EndY=1.5 EndZ=0
    g2: LineSegment StartX=5 StartY=1.5 StartZ=0 EndX=5 EndY=0 EndZ=0
    g3: LineSegment StartX=0 StartY=0 StartZ=0 EndX=5 EndY=0 EndZ=0
  constraints (13):
    c: Vertical(g0)
    c: Distance(g0) = 1.5
    c: Horizontal(g1)
    c: Distance(g1) = 5
    c: Coincident(g1,g0)
    c: Vertical(g2)
    c: Distance(g2) = 1.5
    c: Coincident(g2,g1)
    c: Block(g1)
    c: Block(g2)
    c: Block(g0)
    c: Coincident(g3,g0)
    c: Coincident(g3,g2)
FEATURE [Part::Extrusion] Extrude023  label="solenoidDriverBottomLipTopExtrude015"
  Base = -> Sketch026
  Dir = (0,0.894389,-0.447291)
  DirMode = 2
  FaceMakerClass = Part::FaceMakerBullseye
  LengthFwd = -6.5
  LengthRev = 0
  Placement = pos=(5,-14.15,19.65) rot=(1,0,0;1.5708rad)
  Solid = true
  Symmetric = false
FEATURE [Sketcher::SketchObject] Sketch027
  FullyConstrained = true
  Placement = pos=(0,-14.3,2.37) rot=(-1,0,0;2.03453rad)
  sketch-geometry (5):
    g0: LineSegment StartX=45.5 StartY=-21.2 StartZ=0 EndX=49.5 EndY=-21.2 EndZ=0
    g1: LineSegment StartX=49.5 StartY=0 StartZ=0 EndX=49.5 EndY=-21.2 EndZ=0
    g2: LineSegment StartX=49.5 StartY=0 StartZ=0 EndX=49.5 EndY=1.6 EndZ=0
    g3: LineSegment StartX=45.5 StartY=-21.2 StartZ=0 EndX=45.5 EndY=1.6 EndZ=0
    g4: LineSegment StartX=49.5 StartY=1.6 StartZ=0 EndX=45.5 EndY=1.6 EndZ=0
  constraints (14):
    c: Horizontal(g0)
    c: Distance(g0) = 4
    c: Coincident(g1,g0)
    c: Vertical(g1)
    c: Block(g1)
    c: Vertical(g2)
    c: Distance(g2) = 1.6
    c: Block(g2)
    c: Coincident(g3,g0)
    c: Vertical(g3)
    c: Coincident(g4,g2)
    c: Horizontal(g4)
    c: Block(g0)
    c: Coincident(g3,g4)
FEATURE [Part::Extrusion] Extrude024
  Base = -> Sketch027
  Dir = (0,0.894389,-0.447291)
  DirMode = 2
  FaceMakerClass = Part::FaceMakerBullseye
  LengthFwd = 6.34
  LengthRev = 0
  Placement = pos=(0,-5.59,1) rot=(0,0,1;0rad)
  Solid = true
  Symmetric = false
FEATURE [Part::Fillet] Fillet014  label="solenoidDriverSideBarFillet014"
  Base = -> Extrude024
  Edges = 1 edges r=1.4: [Edge14]
  Placement = pos=(0,0.9,-0.45) rot=(0,0,1;0rad)
FEATURE [Part::Revolution] Revolve  label="mainScrewStandRevolve"
  Angle = 360
  Axis = (0,0,1)
  Base = (0,0,0)
  FaceMakerClass = Part::FaceMakerBullseye
  Placement = pos=(121.35,-15.3,0) rot=(0,0,1;0rad)
  Solid = true
  Source = -> Sketch004
  Symmetric = false
FEATURE [Part::Extrusion] Extrude021  label="solenoidDriverTopLipLowerExtrude011"
  Base = -> Sketch024
  Dir = (0,0.894389,-0.447291)
  DirMode = 2
  FaceMakerClass = Part::FaceMakerBullseye
  LengthFwd = 5.05
  LengthRev = 0
  Solid = true
  Symmetric = false
FEATURE [Part::Fillet] Fillet012  label="solenoidDriverTopLipLowerFillet004"
  Base = -> Extrude021
  Edges = 1 edges r=1.2: [Edge7]
  Placement = pos=(0,-0.9,-1.35) rot=(0,0,1;0rad)
FEATURE [Part::Fillet] Fillet003  label="solenoidDriverTopLipLowerFillet003"
  Base = -> Extrude010
  Edges = 1 edges r=1.2: [Edge7]
  Placement = pos=(0,-3,-0.3) rot=(0,0,1;0rad)
FEATURE [Part::Extrusion] Extrude025  label="mainBodyUpperExtrude025"
  Base = -> Sketch001
  Dir = (0,0,1)
  DirMode = 2
  FaceMakerClass = Part::FaceMakerBullseye
  LengthFwd = 20
  LengthRev = 0
  Solid = true
  Symmetric = false
FEATURE [Part::MultiFuse] Fusion  label="solenoidDriverBottomLipFusion"
  Placement = pos=(0,-1.6,0) rot=(0,0,1;0rad)
  Shapes = -> [Fillet005,Fillet013,Extrude023,Extrude013]
FEATURE [Sketcher::SketchObject] Sketch028
  FullyConstrained = true
  Placement = pos=(0,-14.3,2.37) rot=(-1,0,0;2.03453rad)
  sketch-geometry (4):
    g0: LineSegment StartX=0 StartY=1.5 StartZ=0 EndX=0 EndY=0 EndZ=0
    g1: LineSegment StartX=0 StartY=1.5 StartZ=0 EndX=5 EndY=1.5 EndZ=0
    g2: LineSegment StartX=5 StartY=1.5 StartZ=0 EndX=5 EndY=0 EndZ=0
    g3: LineSegment StartX=0 StartY=0 StartZ=0 EndX=5 EndY=0 EndZ=0
  constraints (13):
    c: Vertical(g0)
    c: Distance(g0) = 1.5
    c: Horizontal(g1)
    c: Distance(g1) = 5
    c: Coincident(g1,g0)
    c: Vertical(g2)
    c: Distance(g2) = 1.5
    c: Coincident(g2,g1)
    c: Block(g1)
    c: Block(g2)
    c: Block(g0)
    c: Coincident(g3,g0)
    c: Coincident(g3,g2)
FEATURE [Part::Extrusion] Extrude026  label="solenoidDriverBottomLipTopExtrude016"
  Base = -> Sketch028
  Dir = (0,0.894389,-0.447291)
  DirMode = 2
  FaceMakerClass = Part::FaceMakerBullseye
  LengthFwd = -6.5
  LengthRev = 0
  Placement = pos=(5,-14.15,19.65) rot=(1,0,0;1.5708rad)
  Solid = true
  Symmetric = false
FEATURE [Sketcher::SketchObject] Sketch029
  FullyConstrained = true
  Placement = pos=(0,-14.3,2.37) rot=(-1,0,0;2.03453rad)
  sketch-geometry (4):
    g0: LineSegment StartX=0 StartY=1.5 StartZ=0 EndX=0 EndY=0 EndZ=0
    g1: LineSegment StartX=0 StartY=1.5 StartZ=0 EndX=5 EndY=1.5 EndZ=0
    g2: LineSegment StartX=5 StartY=1.5 StartZ=0 EndX=5 EndY=0 EndZ=0
    g3: LineSegment StartX=0 StartY=0 StartZ=0 EndX=5 EndY=0 EndZ=0
  constraints (13):
    c: Vertical(g0)
    c: Distance(g0) = 1.5
    c: Horizontal(g1)
    c: Distance(g1) = 5
    c: Coincident(g1,g0)
    c: Vertical(g2)
    c: Distance(g2) = 1.5
    c: Coincident(g2,g1)
    c: Block(g1)
    c: Block(g2)
    c: Block(g0)
    c: Coincident(g3,g0)
    c: Coincident(g3,g2)
FEATURE [Part::Extrusion] Extrude027  label="solenoidDriverBottomLipTopExtrude017"
  Base = -> Sketch029
  Dir = (0,0.894389,-0.447291)
  DirMode = 2
  FaceMakerClass = Part::FaceMakerBullseye
  LengthFwd = -6.5
  LengthRev = 0
  Placement = pos=(0,-14.15,19.65) rot=(1,0,0;1.5708rad)
  Solid = true
  Symmetric = false
FEATURE [Sketcher::SketchObject] Sketch030
  FullyConstrained = true
  Placement = pos=(0,-14.3,2.37) rot=(-1,0,0;2.03453rad)
  sketch-geometry (4):
    g0: LineSegment StartX=0 StartY=1.5 StartZ=0 EndX=0 EndY=0 EndZ=0
    g1: LineSegment StartX=0 StartY=1.5 StartZ=0 EndX=5 EndY=1.5 EndZ=0
    g2: LineSegment StartX=5 StartY=1.5 StartZ=0 EndX=5 EndY=0 EndZ=0
    g3: LineSegment StartX=0 StartY=0 StartZ=0 EndX=5 EndY=0 EndZ=0
  constraints (13):
    c: Vertical(g0)
    c: Distance(g0) = 1.5
    c: Horizontal(g1)
    c: Distance(g1) = 5
    c: Coincident(g1,g0)
    c: Vertical(g2)
    c: Distance(g2) = 1.5
    c: Coincident(g2,g1)
    c: Block(g1)
    c: Block(g2)
    c: Block(g0)
    c: Coincident(g3,g0)
    c: Coincident(g3,g2)
FEATURE [Sketcher::SketchObject] Sketch031
  FullyConstrained = true
  Placement = pos=(0,-14.3,2.37) rot=(-1,0,0;2.03453rad)
  sketch-geometry (6):
    g0: LineSegment StartX=45.5 StartY=-21.2 StartZ=0 EndX=49.5 EndY=-21.2 EndZ=0
    g1: LineSegment StartX=45.5 StartY=0 StartZ=0 EndX=49.5 EndY=0 EndZ=0
    g2: LineSegment StartX=49.5 StartY=0 StartZ=0 EndX=49.5 EndY=-21.2 EndZ=0
    g3: LineSegment StartX=4 StartY=0 StartZ=0 EndX=4 EndY=-21.2 EndZ=0
    g4: LineSegment StartX=45.5 StartY=-21.2 StartZ=0 EndX=4 EndY=-21.2 EndZ=0
    g5: LineSegment StartX=4 StartY=0 StartZ=0 EndX=45.5 EndY=0 EndZ=0
  constraints (16):
    c: Horizontal(g0)
    c: Distance(g0) = 4
    c: Horizontal(g1)
    c: Distance(g1) = 4
    c: Coincident(g2,g1)
    c: Coincident(g2,g0)
    c: Vertical(g2)
    c: Block(g2)
    c: Vertical(g3)
    c: Coincident(g4,g0)
    c: Horizontal(g4)
    c: Coincident(g4,g3)
    c: Coincident(g5,g1)
    c: Horizontal(g5)
    c: Block(g3)
    c: Block(g5)
FEATURE [Part::Extrusion] Extrude028  label="removeFromSolenoidDriverMainExtrude021"
  Base = -> Sketch031
  Dir = (0,0.894389,-0.447291)
  DirMode = 2
  FaceMakerClass = Part::FaceMakerBullseye
  LengthFwd = 3.1
  LengthRev = 0
  Placement = pos=(-4,-2.42,-0.8) rot=(0,0,1;0rad)
  Solid = true
  Symmetric = false
FEATURE [Part::Extrusion] Extrude029  label="solenoidDriverBottomLipTopExtrude018"
  Base = -> Sketch030
  Dir = (0,0.894389,-0.447291)
  DirMode = 2
  FaceMakerClass = Part::FaceMakerBullseye
  LengthFwd = -6.5
  LengthRev = 0
  Placement = pos=(5,-14.15,19.65) rot=(1,0,0;1.5708rad)
  Solid = true
  Symmetric = false
FEATURE [Sketcher::SketchObject] Sketch032
  FullyConstrained = true
  Placement = pos=(0,-14.3,2.37) rot=(-1,0,0;2.03453rad)
  sketch-geometry (4):
    g0: LineSegment StartX=0 StartY=1.5 StartZ=0 EndX=0 EndY=0 EndZ=0
    g1: LineSegment StartX=0 StartY=1.5 StartZ=0 EndX=5 EndY=1.5 EndZ=0
    g2: LineSegment StartX=5 StartY=1.5 StartZ=0 EndX=5 EndY=0 EndZ=0
    g3: LineSegment StartX=0 StartY=0 StartZ=0 EndX=5 EndY=0 EndZ=0
  constraints (13):
    c: Vertical(g0)
    c: Distance(g0) = 1.5
    c: Horizontal(g1)
    c: Distance(g1) = 5
    c: Coincident(g1,g0)
    c: Vertical(g2)
    c: Distance(g2) = 1.5
    c: Coincident(g2,g1)
    c: Block(g1)
    c: Block(g2)
    c: Block(g0)
    c: Coincident(g3,g0)
    c: Coincident(g3,g2)
FEATURE [Part::Extrusion] Extrude030  label="solenoidDriverBottomLipTopExtrude019"
  Base = -> Sketch032
  Dir = (0,0.894389,-0.447291)
  DirMode = 2
  FaceMakerClass = Part::FaceMakerBullseye
  LengthFwd = -6.5
  LengthRev = 0
  Placement = pos=(0,-14.15,19.65) rot=(1,0,0;1.5708rad)
  Solid = true
  Symmetric = false
FEATURE [Part::MultiFuse] Fusion004
  Placement = pos=(0,1.4,2.65) rot=(0,0,1;0rad)
  Shapes = -> [Extrude029,Extrude030]
FEATURE [Part::MultiFuse] Fusion003
  Placement = pos=(-2.3,0,0) rot=(0,0,1;0rad)
  Shapes = -> [Extrude028,Fusion004]
FEATURE [Sketcher::SketchObject] Sketch033
  FullyConstrained = true
  Placement = pos=(0,-14.3,2.37) rot=(-1,0,0;2.03453rad)
  sketch-geometry (4):
    g0: LineSegment StartX=0 StartY=1.5 StartZ=0 EndX=0 EndY=0 EndZ=0
    g1: LineSegment StartX=0 StartY=1.5 StartZ=0 EndX=5 EndY=1.5 EndZ=0
    g2: LineSegment StartX=5 StartY=1.5 StartZ=0 EndX=5 EndY=0 EndZ=0
    g3: LineSegment StartX=0 StartY=0 StartZ=0 EndX=5 EndY=0 EndZ=0
  constraints (13):
    c: Vertical(g0)
    c: Distance(g0) = 1.5
    c: Horizontal(g1)
    c: Distance(g1) = 5
    c: Coincident(g1,g0)
    c: Vertical(g2)
    c: Distance(g2) = 1.5
    c: Coincident(g2,g1)
    c: Block(g1)
    c: Block(g2)
    c: Block(g0)
    c: Coincident(g3,g0)
    c: Coincident(g3,g2)
FEATURE [Sketcher::SketchObject] Sketch034
  FullyConstrained = true
  Placement = pos=(0,-14.3,2.37) rot=(-1,0,0;2.03453rad)
  sketch-geometry (4):
    g0: LineSegment StartX=0 StartY=1.5 StartZ=0 EndX=0 EndY=0 EndZ=0
    g1: LineSegment StartX=0 StartY=1.5 StartZ=0 EndX=5 EndY=1.5 EndZ=0
    g2: LineSegment StartX=5 StartY=1.5 StartZ=0 EndX=5 EndY=0 EndZ=0
    g3: LineSegment StartX=0 StartY=0 StartZ=0 EndX=5 EndY=0 EndZ=0
  constraints (13):
    c: Vertical(g0)
    c: Distance(g0) = 1.5
    c: Horizontal(g1)
    c: Distance(g1) = 5
    c: Coincident(g1,g0)
    c: Vertical(g2)
    c: Distance(g2) = 1.5
    c: Coincident(g2,g1)
    c: Block(g1)
    c: Block(g2)
    c: Block(g0)
    c: Coincident(g3,g0)
    c: Coincident(g3,g2)
FEATURE [Part::Extrusion] Extrude020  label="removeFromSolenoidDriverMainExtrude020"
  Base = -> Sketch020
  Dir = (0,0.894389,-0.447291)
  DirMode = 2
  FaceMakerClass = Part::FaceMakerBullseye
  LengthFwd = 3.1
  LengthRev = 0
  Placement = pos=(-4,-2.42,-0.8) rot=(0,0,1;0rad)
  Solid = true
  Symmetric = false
FEATURE [Part::Fillet] Fillet
  Base = -> Fusion003
  Edges = 1 edges r=10: [Edge5]
  Placement = pos=(-2,0,0) rot=(0,0,1;0rad)
FEATURE [Part::MultiFuse] Fusion001
  Placement = pos=(0,1.4,2.65) rot=(0,0,1;0rad)
  Shapes = -> [Extrude026,Extrude027]
FEATURE [Part::MultiFuse] Fusion002
  Shapes = -> [Extrude020,Fusion001]
FEATURE [Sketcher::SketchObject] Sketch035
  FullyConstrained = true
  Placement = pos=(0,-14.3,2.37) rot=(-1,0,0;2.03453rad)
  sketch-geometry (4):
    g0: LineSegment StartX=0 StartY=1.5 StartZ=0 EndX=0 EndY=0 EndZ=0
    g1: LineSegment StartX=0 StartY=1.5 StartZ=0 EndX=5 EndY=1.5 EndZ=0
    g2: LineSegment StartX=5 StartY=1.5 StartZ=0 EndX=5 EndY=0 EndZ=0
    g3: LineSegment StartX=0 StartY=0 StartZ=0 EndX=5 EndY=0 EndZ=0
  constraints (13):
    c: Vertical(g0)
    c: Distance(g0) = 1.5
    c: Horizontal(g1)
    c: Distance(g1) = 5
    c: Coincident(g1,g0)
    c: Vertical(g2)
    c: Distance(g2) = 1.5
    c: Coincident(g2,g1)
    c: Block(g1)
    c: Block(g2)
    c: Block(g0)
    c: Coincident(g3,g0)
    c: Coincident(g3,g2)
FEATURE [Sketcher::SketchObject] Sketch036
  FullyConstrained = true
  Placement = pos=(0,-14.3,2.37) rot=(-1,0,0;2.03453rad)
  sketch-geometry (4):
    g0: LineSegment StartX=0 StartY=1.5 StartZ=0 EndX=0 EndY=0 EndZ=0
    g1: LineSegment StartX=0 StartY=1.5 StartZ=0 EndX=5 EndY=1.5 EndZ=0
    g2: LineSegment StartX=5 StartY=1.5 StartZ=0 EndX=5 EndY=0 EndZ=0
    g3: LineSegment StartX=0 StartY=0 StartZ=0 EndX=5 EndY=0 EndZ=0
  constraints (13):
    c: Vertical(g0)
    c: Distance(g0) = 1.5
    c: Horizontal(g1)
    c: Distance(g1) = 5
    c: Coincident(g1,g0)
    c: Vertical(g2)
    c: Distance(g2) = 1.5
    c: Coincident(g2,g1)
    c: Block(g1)
    c: Block(g2)
    c: Block(g0)
    c: Coincident(g3,g0)
    c: Coincident(g3,g2)
FEATURE [Part::Extrusion] Extrude031  label="solenoidDriverBottomLipTopExtrude020"
  Base = -> Sketch035
  Dir = (0,0.894389,-0.447291)
  DirMode = 2
  FaceMakerClass = Part::FaceMakerBullseye
  LengthFwd = -6.5
  LengthRev = 0
  Placement = pos=(5,-14.15,19.65) rot=(1,0,0;1.5708rad)
  Solid = true
  Symmetric = false
FEATURE [Part::Extrusion] Extrude032  label="solenoidDriverBottomLipTopExtrude021"
  Base = -> Sketch036
  Dir = (0,0.894389,-0.447291)
  DirMode = 2
  FaceMakerClass = Part::FaceMakerBullseye
  LengthFwd = -6.5
  LengthRev = 0
  Placement = pos=(0,-14.15,19.65) rot=(1,0,0;1.5708rad)
  Solid = true
  Symmetric = false
FEATURE [Part::MultiFuse] Fusion009
  Placement = pos=(8,1.4,2.65) rot=(0,0,1;0rad)
  Shapes = -> [Extrude031,Extrude032]
FEATURE [Part::MultiFuse] Fusion010  label="removeFromSolenoidDriver"
  Shapes = -> [Fusion009,Fillet,Fusion002]
FEATURE [Sketcher::SketchObject] Sketch037
  FullyConstrained = true
  Placement = pos=(0,0,0) rot=(1,0,0;1.5708rad)
  sketch-geometry (4):
    g0: Circle CenterX=64.05 CenterY=16.5 CenterZ=0 NormalX=0 NormalY=0 NormalZ=1 AngleXU=0 Radius=2.7
    g1: Circle CenterX=64.05 CenterY=8.5 CenterZ=0 NormalX=0 NormalY=0 NormalZ=1 AngleXU=0 Radius=2.7
    g2: Circle CenterX=84.15 CenterY=8.5 CenterZ=0 NormalX=0 NormalY=0 NormalZ=1 AngleXU=0 Radius=2.7
    g3: Circle CenterX=84.15 CenterY=16.5 CenterZ=0 NormalX=0 NormalY=0 NormalZ=1 AngleXU=0 Radius=2.7
  constraints (4):
    c: Block(g2)
    c: Block(g3)
    c: Block(g0)
    c: Block(g1)
FEATURE [Part::Extrusion] Extrude033  label="removeFromMainBodyToCreateScrewHoleCounterSinks001"
  Base = -> Sketch037
  Dir = (0,-1,1.1e-15)
  DirMode = 2
  FaceMakerClass = Part::FaceMakerBullseye
  LengthFwd = 1.9
  LengthRev = 0
  Placement = pos=(0.8,0,0) rot=(0,0,1;0rad)
  Solid = true
  Symmetric = false
FEATURE [Part::MultiFuse] Fusion011  label="removeFromMainBodyToCreateScrewHoleCounterSinks001Fusion011"
  Shapes = -> [Extrude014,Extrude033]
FEATURE [Sketcher::SketchObject] Sketch038
  FullyConstrained = true
  Placement = pos=(0,-14.3,2.37) rot=(-1,0,0;2.03453rad)
  sketch-geometry (4):
    g0: LineSegment StartX=33.9 StartY=-9.7 StartZ=0 EndX=33.9 EndY=-1.5 EndZ=0
    g1: LineSegment StartX=33.9 StartY=-1.5 StartZ=0 EndX=44.5 EndY=-1.5 EndZ=0
    g2: LineSegment StartX=33.9 StartY=-9.7 StartZ=0 EndX=44.5 EndY=-9.7 EndZ=0
    g3: LineSegment StartX=44.5 StartY=-1.5 StartZ=0 EndX=44.5 EndY=-9.7 EndZ=0
  constraints (10):
    c: Vertical(g0)
    c: Coincident(g1,g0)
    c: Horizontal(g1)
    c: Block(g1)
    c: Block(g0)
    c: Coincident(g2,g0)
    c: Horizontal(g2)
    c: Coincident(g3,g1)
    c: Coincident(g3,g2)
    c: Vertical(g3)
FEATURE [Part::Extrusion] Extrude034
  Base = -> Sketch038
  Dir = (0,0.894389,-0.447291)
  DirMode = 2
  FaceMakerClass = Part::FaceMakerBullseye
  LengthFwd = 16
  LengthRev = 0
  Placement = pos=(0,-22,7) rot=(0,0,1;0rad)
  Solid = true
  Symmetric = false
FEATURE [Sketcher::SketchObject] Sketch039
  FullyConstrained = true
  Placement = pos=(0,-14.3,2.37) rot=(-1,0,0;2.03453rad)
  sketch-geometry (4):
    g0: LineSegment StartX=5.5 StartY=-7.7 StartZ=0 EndX=13.3 EndY=-7.7 EndZ=0
    g1: LineSegment StartX=13.3 StartY=-7.7 StartZ=0 EndX=13.3 EndY=-13.1 EndZ=0
    g2: LineSegment StartX=13.3 StartY=-13.1 StartZ=0 EndX=5.5 EndY=-13.1 EndZ=0
    g3: LineSegment StartX=5.5 StartY=-7.7 StartZ=0 EndX=5.5 EndY=-13.1 EndZ=0
  constraints (12):
    c: Horizontal(g0)
    c: Distance(g0) = 7.8
    c: Coincident(g1,g0)
    c: Vertical(g1)
    c: Distance(g1) = 5.4
    c: Coincident(g2,g1)
    c: Horizontal(g2)
    c: Vertical(g3)
    c: Coincident(g3,g2)
    c: Block(g0)
    c: Block(g2)
    c: Block(g3)
FEATURE [Part::Extrusion] Extrude035  label="removeToMakeHoleForConnectorExtrude035"
  Base = -> Sketch039
  Dir = (0,0.894389,-0.447291)
  DirMode = 2
  FaceMakerClass = Part::FaceMakerBullseye
  LengthFwd = 15
  LengthRev = 0
  Placement = pos=(-4,-22,9.6469) rot=(0,0,1;0rad)
  Solid = true
  Symmetric = false
FEATURE [App::MeasureDistance] Distance  label="Distance: 4.00 mm"
  Distance = 4.00184
  P1 = (119.349,-15.3,8)
  P2 = (123.351,-15.3,8)
FEATURE [App::MeasureDistance] Distance001  label="Distance: 3.80 mm"
  Distance = 3.8
  P1 = (119.45,-15.3,8)
  P2 = (123.25,-15.3,8)
FEATURE [Part::Fillet] Fillet015
  Base = -> Extrude009
  Edges = 1 edges r=1.59: [Edge7]
FEATURE [Part::Fillet] Fillet016
  Base = -> Extrude017
  Edges = 1 edges r=1.49: [Edge12]
FEATURE [Part::Fillet] Fillet017
  Base = -> Fillet016
  Edges = 1 edges r=1.45: [Edge8]
FEATURE [Part::MultiFuse] Fusion012  label="main"
  Shapes = -> [Extrude,Revolve,Extrude005,Fillet003,Fillet012,Fillet014,Extrude025,Fusion,Fillet015,Fillet017]
FEATURE [Part::Cut] Cut001
  Base = -> Fusion012
  Tool = -> Box003
FEATURE [Part::Cut] Cut002
  Base = -> Cut001
  Tool = -> Box002
FEATURE [Part::Cut] Cut003
  Base = -> Cut002
  Tool = -> Cut
FEATURE [Part::Cut] Cut004
  Base = -> Cut003
  Tool = -> Extrude019
FEATURE [Part::Cut] Cut005
  Base = -> Cut004
  Tool = -> Fusion011
FEATURE [Part::Cut] Cut006
  Base = -> Cut005
  Tool = -> Extrude004
FEATURE [Part::Cut] Cut007
  Base = -> Cut006
  Tool = -> Extrude015
FEATURE [Part::Cut] Cut008
  Base = -> Cut007
  Tool = -> Extrude008
FEATURE [Part::Cut] Cut009
  Base = -> Cut008
  Tool = -> Fusion010
FEATURE [App::MeasureDistance] Distance002  label="Distance: 2.05 mm"
  Distance = 2.05453
  P1 = (1.5,-23.0732,21.402)
  P2 = (6e-15,-23,20)
FEATURE [Part::Cut] Cut010
  Base = -> Cut009
  Tool = -> Extrude035
FEATURE [Part::Cut] Cut011
  Base = -> Cut010
  Tool = -> Extrude034
FEATURE [Part::Fillet] Fillet018
  Base = -> Cut011
  Edges = 1 edges r=3: [Edge134]
FEATURE [Part::Fillet] Fillet019
  Base = -> Fillet018
  Edges = 1 edges r=3: [Edge29]
FEATURE [Part::Box] Box004  label="Cube004"
  AttacherType = Attacher::AttachEngine3D
  Height = 10
  Length = 200
  Placement = pos=(-30,0,0) rot=(0,0,1;0rad)
  Width = 10
FEATURE [Part::Fillet] Fillet020
  Base = -> Box004
  Edges = 1 edges r=3.6: [Edge12]
FEATURE [Part::Box] Box005  label="Cube005"
  AttacherType = Attacher::AttachEngine3D
  Height = 10
  Length = 198
  Placement = pos=(-30,0,0) rot=(0,0,1;0rad)
  Width = 10
FEATURE [Part::Cut] Cut012
  Base = -> Box005
  Tool = -> Fillet020
FEATURE [Part::Box] Box006  label="Cube006"
  AttacherType = Attacher::AttachEngine3D
  Height = 5
  Length = 200
  Placement = pos=(-30,6.4,10) rot=(1,0,0;0rad)
  Width = 5
FEATURE [Part::Box] Box007  label="Cube007"
  AttacherType = Attacher::AttachEngine3D
  Height = 5
  Length = 200
  Placement = pos=(-30,6.4,10) rot=(1,0,0;0.872665rad)
  Width = 5
FEATURE [Part::MultiFuse] Fusion013  label="removeFromMainFusion013"
  Placement = pos=(0,-10,10) rot=(0,0,1;0rad)
  Shapes = -> [Box007,Box006,Cut012]
FEATURE [Part::Cut] Cut013
  Base = -> Fillet019
  Tool = -> Fusion013
FEATURE [Mesh::Feature] v0_98_Cut013  label="v0_98-Cut013"
FEATURE [App::MeasureDistance] Distance003  label="Distance: 7.18 mm"
  Distance = 7.17719
  P1 = (117.773,-15.3145,-2.4)
  P2 = (124.951,-15.2973,-2.4)
FEATURE [Sketcher::SketchObject] Sketch040
  FullyConstrained = true
  Placement = pos=(0,-14.3,2.37) rot=(-1,0,0;2.03453rad)
  sketch-geometry (4):
    g0: LineSegment StartX=0 StartY=1.5 StartZ=0 EndX=0 EndY=0 EndZ=0
    g1: LineSegment StartX=0 StartY=1.5 StartZ=0 EndX=5 EndY=1.5 EndZ=0
    g2: LineSegment StartX=5 StartY=1.5 StartZ=0 EndX=5 EndY=0 EndZ=0
    g3: LineSegment StartX=0 StartY=0 StartZ=0 EndX=5 EndY=0 EndZ=0
  constraints (13):
    c: Vertical(g0)
    c: Distance(g0) = 1.5
    c: Horizontal(g1)
    c: Distance(g1) = 5
    c: Coincident(g1,g0)
    c: Vertical(g2)
    c: Distance(g2) = 1.5
    c: Coincident(g2,g1)
    c: Block(g1)
    c: Block(g2)
    c: Block(g0)
    c: Coincident(g3,g0)
    c: Coincident(g3,g2)
FEATURE [Part::Extrusion] Extrude036
  Base = -> Sketch040
  Dir = (0,0.894389,-0.447291)
  DirMode = 2
  FaceMakerClass = Part::FaceMakerBullseye
  LengthFwd = 1.4
  LengthRev = 0
  Placement = pos=(0,8.25,17.58) rot=(0,0,1;0rad)
  Solid = true
  Symmetric = false
FEATURE [Sketcher::SketchObject] Sketch041
  FullyConstrained = true
  Placement = pos=(0,-14.3,2.37) rot=(-1,0,0;2.03453rad)
  sketch-geometry (4):
    g0: LineSegment StartX=0 StartY=1.5 StartZ=0 EndX=0 EndY=0 EndZ=0
    g1: LineSegment StartX=0 StartY=1.5 StartZ=0 EndX=5 EndY=1.5 EndZ=0
    g2: LineSegment StartX=5 StartY=1.5 StartZ=0 EndX=5 EndY=0 EndZ=0
    g3: LineSegment StartX=0 StartY=0 StartZ=0 EndX=5 EndY=0 EndZ=0
  constraints (13):
    c: Vertical(g0)
    c: Distance(g0) = 1.5
    c: Horizontal(g1)
    c: Distance(g1) = 5
    c: Coincident(g1,g0)
    c: Vertical(g2)
    c: Distance(g2) = 1.5
    c: Coincident(g2,g1)
    c: Block(g1)
    c: Block(g2)
    c: Block(g0)
    c: Coincident(g3,g0)
    c: Coincident(g3,g2)
FEATURE [Part::Extrusion] Extrude037
  Base = -> Sketch041
  Dir = (0,0.894389,-0.447291)
  DirMode = 2
  FaceMakerClass = Part::FaceMakerBullseye
  LengthFwd = 1.4
  LengthRev = 0
  Placement = pos=(0,6.11,13.33) rot=(0,0,1;0rad)
  Solid = true
  Symmetric = false
FEATURE [Part::MultiFuse] Fusion014  label="screwSpacerFusion014"
  Shapes = -> [Extrude037,Extrude036]
FEATURE [Sketcher::SketchObject] Sketch042
  FullyConstrained = true
  Placement = pos=(0,-14.3,2.37) rot=(-1,0,0;2.03453rad)
  sketch-geometry (4):
    g0: LineSegment StartX=0 StartY=1.5 StartZ=0 EndX=0 EndY=0 EndZ=0
    g1: LineSegment StartX=0 StartY=1.5 StartZ=0 EndX=5 EndY=1.5 EndZ=0
    g2: LineSegment StartX=5 StartY=1.5 StartZ=0 EndX=5 EndY=0 EndZ=0
    g3: LineSegment StartX=0 StartY=0 StartZ=0 EndX=5 EndY=0 EndZ=0
  constraints (13):
    c: Vertical(g0)
    c: Distance(g0) = 1.5
    c: Horizontal(g1)
    c: Distance(g1) = 5
    c: Coincident(g1,g0)
    c: Vertical(g2)
    c: Distance(g2) = 1.5
    c: Coincident(g2,g1)
    c: Block(g1)
    c: Block(g2)
    c: Block(g0)
    c: Coincident(g3,g0)
    c: Coincident(g3,g2)
FEATURE [Part::Extrusion] Extrude038
  Base = -> Sketch042
  Dir = (0,0.894389,-0.447291)
  DirMode = 2
  FaceMakerClass = Part::FaceMakerBullseye
  LengthFwd = 1.4
  LengthRev = 0
  Placement = pos=(0,8.459,18) rot=(0,0,1;0rad)
  Solid = true
  Symmetric = false
FEATURE [Part::MultiFuse] Fusion015  label="screwSpacerFusion014Fusion015"
  Placement = pos=(0,0.35,-0.18) rot=(0,0,1;0rad)
  Shapes = -> [Extrude038,Fusion014]
FEATURE [Part::Cylinder] Cylinder
  Angle = 360
  AttacherType = Attacher::AttachEngine3D
  Height = 10
  Placement = pos=(0,10,0) rot=(0,0,1;0rad)
  Radius = 1.5
FEATURE [Part::Cylinder] Cylinder001
  Angle = 360
  AttacherType = Attacher::AttachEngine3D
  Height = 10
  Placement = pos=(3,10,0) rot=(0,0,1;0rad)
  Radius = 1.5
FEATURE [Part::Box] Box008  label="Cube008"
  AttacherType = Attacher::AttachEngine3D
  Height = 10
  Length = 3
  Placement = pos=(0,8.5,0) rot=(0,0,1;0rad)
  Width = 3
FEATURE [Part::MultiFuse] Fusion016  label="holeForWireFusion016"
  Shapes = -> [Cylinder001,Box008,Cylinder]
FEATURE [Part::Box] Box009  label="Cube009"
  AttacherType = Attacher::AttachEngine3D
  Height = 10
  Length = 3
  Placement = pos=(0,8.5,0) rot=(0,0,1;0rad)
  Width = 3
FEATURE [Part::Cylinder] Cylinder002
  Angle = 360
  AttacherType = Attacher::AttachEngine3D
  Height = 10
  Placement = pos=(0,10,0) rot=(0,0,1;0rad)
  Radius = 1.5
FEATURE [Part::Cylinder] Cylinder003
  Angle = 360
  AttacherType = Attacher::AttachEngine3D
  Height = 10
  Placement = pos=(3,10,0) rot=(0,0,1;0rad)
  Radius = 1.5
FEATURE [Part::MultiFuse] Fusion017  label="holeForWireFusion017"
  Placement = pos=(0,0,10) rot=(0,0,1;0rad)
  Shapes = -> [Cylinder003,Box009,Cylinder002]
FEATURE [Part::MultiFuse] Fusion018  label="holeForWireFusion018"
  Placement = pos=(0,0,0) rot=(0,1,0;-1.5708rad)
  Shapes = -> [Fusion017,Fusion016]
FEATURE [Part::Box] Box010  label="Cube010"
  AttacherType = Attacher::AttachEngine3D
  Height = 0.1
  Length = 0.1
  Placement = pos=(-2,10,0) rot=(0,0.995037,0.099504;0rad)
  Width = 0.1
FEATURE [Part::MultiFuse] Fusion019
  Placement = pos=(0,10,0) rot=(1,0,0;1.5708rad)
  Shapes = -> [Box010,Fusion018]
FEATURE [Part::Box] Box011  label="Cube011"
  AttacherType = Attacher::AttachEngine3D
  Height = 0.1
  Length = 1.1
  Placement = pos=(-2,10,10) rot=(0,0.995037,0.099504;0rad)
  Width = 0.1
FEATURE [Part::MultiFuse] Fusion020
  Placement = pos=(0,0,0) rot=(0,1,0;0.349066rad)
  Shapes = -> [Box011,Fusion019]
FEATURE [Part::Box] Box012  label="Cube012"
  AttacherType = Attacher::AttachEngine3D
  Height = 0.1
  Length = 1.1
  Placement = pos=(-2,10,10) rot=(0,0.995037,0.099504;0rad)
  Width = 0.1
FEATURE [Part::MultiFuse] Fusion021
  Placement = pos=(0,30,0) rot=(0,0,1;-2.6529rad)
  Shapes = -> [Box012,Fusion020]
FEATURE [Part::Box] Box013  label="Cube013"
  AttacherType = Attacher::AttachEngine3D
  Height = 0.1
  Length = 1.1
  Placement = pos=(2,19,10) rot=(0,0.995037,0.099504;0rad)
  Width = 0.1
FEATURE [Part::MultiFuse] Fusion022  label="holeForWire"
  Placement = pos=(15,-49.8,-8.2) rot=(0,0,1;0rad)
  Shapes = -> [Box013,Fusion021]
